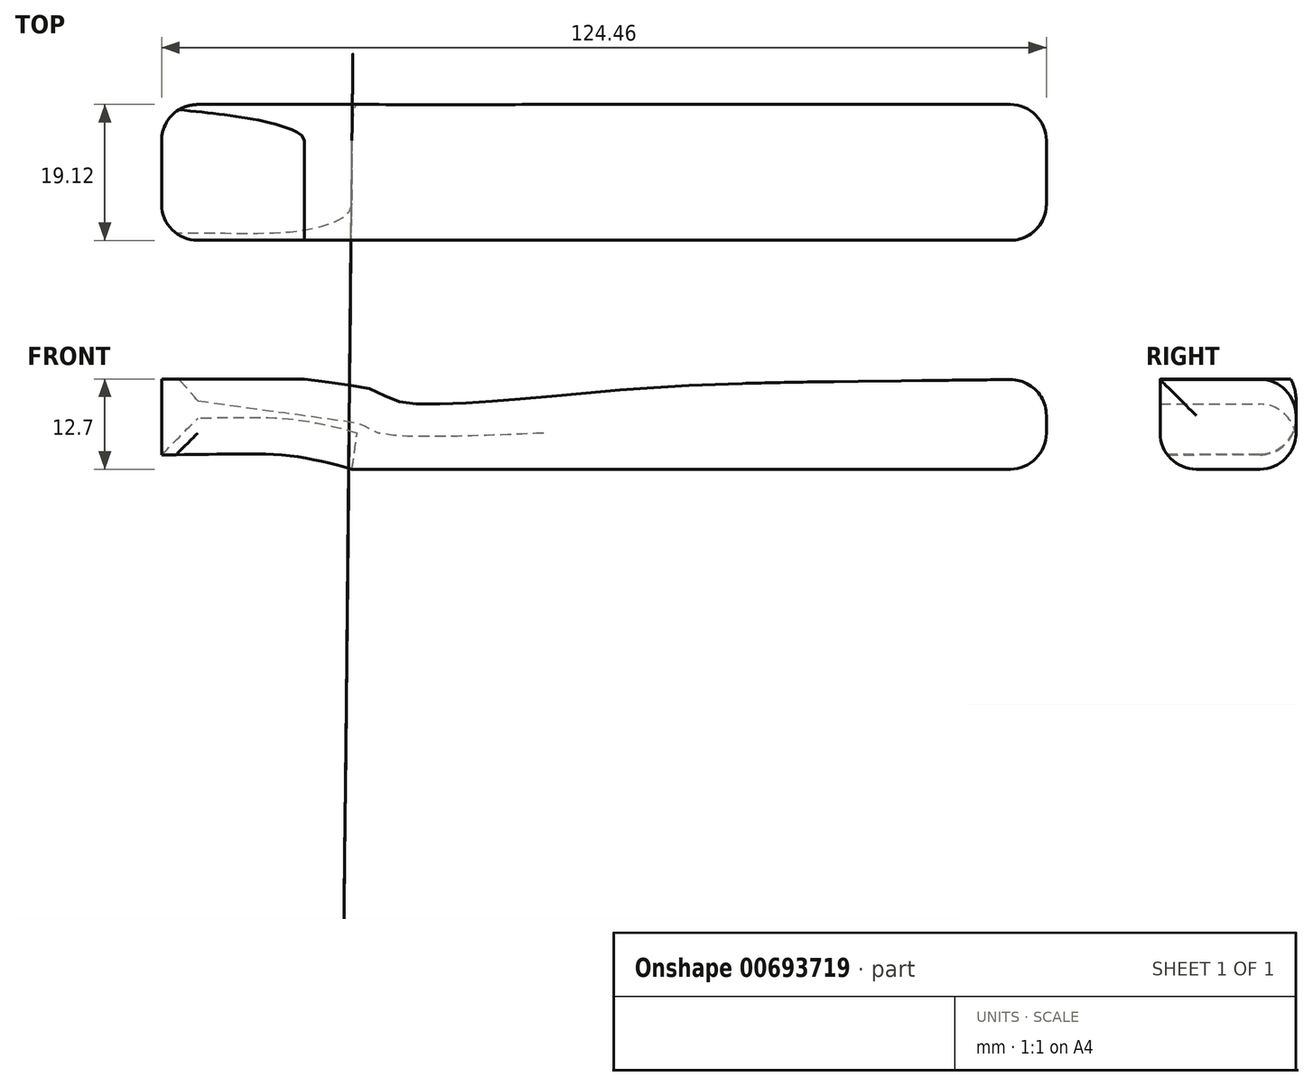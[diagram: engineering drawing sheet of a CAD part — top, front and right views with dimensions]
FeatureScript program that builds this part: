
annotation { "Feature Type Name" : "Feature", "Feature Type Description" : "" }
export const myFeature = defineFeature(function(context is Context, id is Id, definition is map)
    precondition{}
    {
        {
            var Q0;
            Q0=qCreatedBy(makeId("Top.planeOp"),FACE);
            var sketch = newSketch(context, id + "F0", { "sketchPlane" : qUnion([Q0])});
            skLineSegment(sketch, "E0.bottom", {"start": v(-62.34, -25.23) * mm, "end": v(62.12, -25.23) * mm});
            skLineSegment(sketch, "E0.top", {"start": v(-62.34, -6.11) * mm, "end": v(62.12, -6.11) * mm});
            skLineSegment(sketch, "E0.left", {"start": v(-62.34, -25.23) * mm, "end": v(-62.34, -6.11) * mm});
            skLineSegment(sketch, "E0.right", {"start": v(62.12, -25.23) * mm, "end": v(62.12, -6.11) * mm});
            skSolve(sketch);
        }
        {
            var Q0;
            Q0=makeQuery(id+"F0.imprint","IMPRINT",FACE,{"disambiguationData":[TD([[makeQuery(id+"F0.imprint","IMPRINT",EDGE,{"derivedFrom":sQuery(id+"F0.wireOp",EDGE,"E0.bottom")}),1.0]])]});
            extrude(context, id + "F1", {"entities" : qUnion([Q0]), "depth" : 12.7 * mm, "offsetDistance" : 25.4 * mm});
        }
        {
            var Q0;
            Q0=makeQuery(id+"F1.opExtrude","SWEPT_FACE",FACE,{"disambiguationData":[OSD([sQuery(id+"F0.wireOp",EDGE,"E0.bottom")])]});
            var sketch = newSketch(context, id + "F2", { "sketchPlane" : qUnion([Q0])});
            skFitSpline(sketch, "E1", {"points": [v(-42.26, 12.7) * mm, v(-36.07, 11.85) * mm, v(-32.43, 11.07) * mm, v(-29.77, 9.75) * mm, v(-26.79, 9.2) * mm, v(-20.16, 9.3) * mm, v(-12.2, 9.86) * mm, v(0, 10.96) * mm, v(13.34, 11.85) * mm, v(33.35, 12.34) * mm, v(51.51, 12.55) * mm, v(62.12, 12.7) * mm], "startDerivative": vector(85.12, -11.76) * mm, "endDerivative": vector(98.93, 1.53) * mm});
            skSolve(sketch);
        }
        {
            var Q0;
            {var subQ0=sQuery(id+"F2.wireOp",EDGE,"E1");Q0=makeQuery(id+"F2.imprint","IMPRINT",FACE,{"disambiguationData":[TD([[makeQuery(id+"F2.imprint","IMPRINT",EDGE,{"derivedFrom":subQ0}),1.0]])]});}
            extrude(context, id + "F3", {"entities" : qUnion([Q0]), "operationType" : NewBodyOperationType.REMOVE, "oppositeDirection" : true, "depth" : 25.4 * mm, "offsetDistance" : 25.4 * mm});
        }
        {
            var Q0;
            Q0=makeQuery(id+"F1.opExtrude","SWEPT_FACE",FACE,{"disambiguationData":[OSD([sQuery(id+"F0.wireOp",EDGE,"E0.bottom")])]});
            var sketch = newSketch(context, id + "F4", { "sketchPlane" : qUnion([Q0])});
            skFitSpline(sketch, "E2", {"points": [v(-62.34, 2.01) * mm, v(-50.95, 2.14) * mm, v(-41.81, 1.5) * mm, v(-35.56, 0) * mm, v(-35.56, 0) * mm], "startDerivative": vector(31.73, 0.42) * mm, "endDerivative": vector(-0.47, 0.05) * mm});
            skSolve(sketch);
        }
        {
            var Q0;
            {var subQ0=sQuery(id+"F4.wireOp",EDGE,"E2");var subQ1=sQuery(id+"F0.wireOp",EDGE,"E0.bottom");var subQ2=makeQuery(id+"F1.opExtrude","CAP_EDGE",EDGE,{"disambiguationData":[OSD([subQ1])],"isStart":true});var subQ3=makeQuery(id+"F4.imprint","INTERSECT",VERTEX,{"disambiguationData":[OD(0.0)],"derivedFrom":[subQ2,subQ0]});Q0=makeQuery(id+"F4.imprint","IMPRINT",FACE,{"disambiguationData":[TD([[makeQuery(id+"F4.imprint","IMPRINT",EDGE,{"disambiguationData":[TD([[subQ3,-1.0]])],"derivedFrom":subQ0}),1.0]])]});}
            extrude(context, id + "F5", {"entities" : qUnion([Q0]), "operationType" : NewBodyOperationType.REMOVE, "oppositeDirection" : true, "depth" : 25.4 * mm, "offsetDistance" : 25.4 * mm});
        }
        {
            var Q0;
            Q0=makeQuery(id+"F3.boolean.opBoolean","COPY",EDGE,{"derivedFrom":makeQuery(id+"F3.opExtrude","CAP_EDGE",EDGE,{"disambiguationData":[OSD([sQuery(id+"F2.wireOp",EDGE,"E1")])],"isStart":true})});
            var Q1;
            Q1=makeQuery(id+"F1.opExtrude","SWEPT_EDGE",EDGE,{"disambiguationData":[OSD([sQuery(id+"F0.wireOp",EDGE,"E0.bottom"),sQuery(id+"F0.wireOp",EDGE,"E0.right")])]});
            var Q2;
            {var subQ0=sQuery(id+"F0.wireOp",EDGE,"E0.right");Q2=makeQuery(id+"F3.boolean.opBoolean","MERGE",EDGE,{"derivedFrom":[makeQuery(id+"F1.opExtrude","CAP_EDGE",EDGE,{"disambiguationData":[OSD([subQ0])],"isStart":false}),makeQuery(id+"F3.opExtrude","SWEPT_EDGE",EDGE,{"disambiguationData":[OSD([sQuery(id+"F0.wireOp",EDGE,"E0.bottom"),subQ0,sQuery(id+"F2.wireOp",EDGE,"E1")])]})]});}
            var Q3;
            Q3=makeQuery(id+"F1.opExtrude","SWEPT_EDGE",EDGE,{"disambiguationData":[OSD([sQuery(id+"F0.wireOp",EDGE,"E0.top"),sQuery(id+"F0.wireOp",EDGE,"E0.right")])]});
            var Q4;
            Q4=makeQuery(id+"F1.opExtrude","CAP_EDGE",EDGE,{"disambiguationData":[OSD([sQuery(id+"F0.wireOp",EDGE,"E0.right")])],"isStart":true});
            var Q5;
            Q5=makeQuery(id+"F1.opExtrude","CAP_EDGE",EDGE,{"disambiguationData":[OSD([sQuery(id+"F0.wireOp",EDGE,"E0.top")])],"isStart":true});
            var Q6;
            Q6=makeQuery(id+"F5.boolean.opBoolean","INTERSECT",EDGE,{"derivedFrom":[makeQuery(id+"F1.opExtrude","SWEPT_FACE",FACE,{"disambiguationData":[OSD([sQuery(id+"F0.wireOp",EDGE,"E0.top")])]}),makeQuery(id+"F5.opExtrude","SWEPT_FACE",FACE,{"disambiguationData":[OSD([sQuery(id+"F4.wireOp",EDGE,"E2")])]})]});
            var Q7;
            Q7=makeQuery(id+"F5.boolean.opBoolean","COPY",EDGE,{"derivedFrom":makeQuery(id+"F5.opExtrude","CAP_EDGE",EDGE,{"disambiguationData":[OSD([sQuery(id+"F4.wireOp",EDGE,"E2")])],"isStart":true})});
            var Q8;
            Q8=makeQuery(id+"F5.boolean.opBoolean","COPY",EDGE,{"derivedFrom":makeQuery(id+"F5.opExtrude","SWEPT_EDGE",EDGE,{"disambiguationData":[OSD([sQuery(id+"F0.wireOp",EDGE,"E0.bottom"),sQuery(id+"F0.wireOp",EDGE,"E0.left"),sQuery(id+"F4.wireOp",EDGE,"E2")])]})});
            var Q9;
            Q9=makeQuery(id+"F1.opExtrude","SWEPT_EDGE",EDGE,{"disambiguationData":[OSD([sQuery(id+"F0.wireOp",EDGE,"E0.bottom"),sQuery(id+"F0.wireOp",EDGE,"E0.left")])]});
            var Q10;
            Q10=makeQuery(id+"F1.opExtrude","SWEPT_EDGE",EDGE,{"disambiguationData":[OSD([sQuery(id+"F0.wireOp",EDGE,"E0.top"),sQuery(id+"F0.wireOp",EDGE,"E0.left")])]});
            var Q11;
            Q11=makeQuery(id+"F5.boolean.opBoolean","COPY",EDGE,{"derivedFrom":makeQuery(id+"F5.opExtrude","SWEPT_EDGE",EDGE,{"disambiguationData":[OSD([sQuery(id+"F0.wireOp",EDGE,"E0.bottom"),sQuery(id+"F4.wireOp",EDGE,"E2")])]})});
            var Q12;
            Q12=makeQuery(id+"F1.opExtrude","CAP_EDGE",EDGE,{"disambiguationData":[OSD([sQuery(id+"F0.wireOp",EDGE,"E0.bottom")])],"isStart":true});
            var Q13;
            Q13=makeQuery(id+"F3.boolean.opBoolean","COPY",EDGE,{"derivedFrom":makeQuery(id+"F3.opExtrude","SWEPT_EDGE",EDGE,{"disambiguationData":[OSD([sQuery(id+"F0.wireOp",EDGE,"E0.bottom"),sQuery(id+"F2.wireOp",EDGE,"E1")])]})});
            var Q14;
            Q14=makeQuery(id+"F3.boolean.opBoolean","INTERSECT",EDGE,{"derivedFrom":[makeQuery(id+"F1.opExtrude","SWEPT_FACE",FACE,{"disambiguationData":[OSD([sQuery(id+"F0.wireOp",EDGE,"E0.top")])]}),makeQuery(id+"F3.opExtrude","SWEPT_FACE",FACE,{"disambiguationData":[OSD([sQuery(id+"F2.wireOp",EDGE,"E1")])]})]});
            fillet(context, id + "F6", {"entities" : qUnion([Q0, Q1, Q2, Q3, Q4, Q5, Q6, Q7, Q8, Q9, Q10, Q11, Q12, Q13, Q14]), "radius" : 5.08 * mm, "tangentPropagation" : true, "allowEdgeOverflow" : false});
        }
    });
